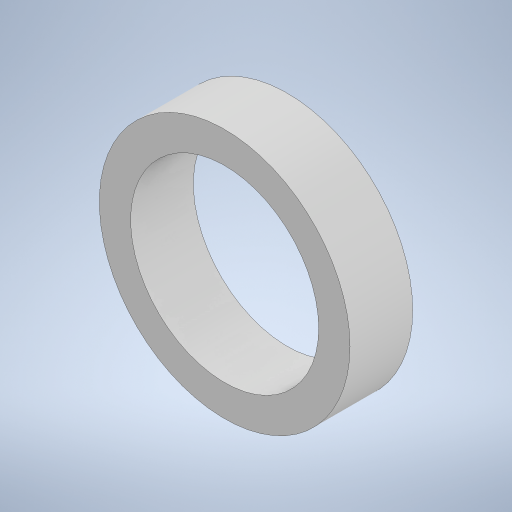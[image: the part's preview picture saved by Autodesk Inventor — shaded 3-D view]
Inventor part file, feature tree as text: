
AUTODESK INVENTOR PART (.ipt)
format: ipt  version: 2023 (Build 270158000, 158)  size: 227,328 bytes
history: native  units: in
note: dims shown in document units (in); Inventor stores cm internally (conversion verified against a paired STEP export)
features: extrude x2, sketch x2
ambient origin geometry x8: Origin, YZ Plane, XZ Plane, XY Plane, X Axis, Y Axis, Z Axis, Center Point
bodies: Solid1 (feature_tree)
feature tree (4):
  extrude  "Extrusion1"  Depth=0.315in
  extrude  "Extrusion2"  Depth=0.0787in
  sketch  "Sketch1"  dims[d0=0.2362in d1=0.315in]
  sketch  "Sketch2"  dims[d2=0.0787in d3=0.0in d4=0.2362in d5=0.0787in d6=0.0in]
